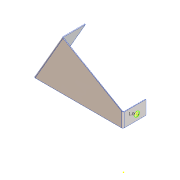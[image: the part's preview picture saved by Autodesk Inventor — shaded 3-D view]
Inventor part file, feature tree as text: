
AUTODESK INVENTOR PART (.ipt)
format: ipt  version: 2016 (Build 200138000, 138)  size: 200,704 bytes
history: native  units: in
note: dims shown in document units (in); Inventor stores cm internally (conversion verified against a paired STEP export)
features: reference x11, sheet_metal_op x7, sketch x6, other x6, fillet x1
ambient origin geometry x8: Origin, YZ Plane, XZ Plane, XY Plane, X Axis, Y Axis, Z Axis, Center Point
bodies: Solid1 (feature_tree)
feature tree (31):
  sheet_metal_op  "Face1"
  sheet_metal_op  "Flange1"
  sketch  "Sketch5"  dims[d8=3.0in]
  sheet_metal_op  "Flange2"
  fillet  "Fillet1"  Radius=30.0in
  sketch  "Sketch7"  dims[d10=90.0deg d11=13.0167in d12=0.125in d13=0.0in d14=0.125in d15=0.0625in d16=0.25in d17=0.125in d18=5.0in d19=90.0deg d20=0.125in d21=0.5in d22=0.125in d23=0.125in d24=0.125in d25=0.0625in d26=0.25in d27=0.125in d28=5.0in d29=90.0deg d30=0.125in d31=0.5in d32=0.125in d33=0.125in d36=1.063in d37=0.125in d38=0.0in d39=0.125in]
  sketch  "Sketch1"  dims[d1=30.0in]
  other  "Plate1"
  sketch  "Sketch3"  dims[d2=0.125in]
  reference  "Reference12"
  reference  "Reference13"
  reference  "Reference14"
  sketch  "Sketch4"  dims[d7=60.0deg]
  other  "Plate2"
  sheet_metal_op  "Bend1"
  sheet_metal_op  "Corner1"
  reference  "Reference15"
  reference  "Reference16"
  reference  "Reference17"
  sketch  "Sketch6"  dims[d9=180.0deg]
  other  "Plate3"
  sheet_metal_op  "Bend2"
  sheet_metal_op  "Corner2"
  reference  "Reference18"
  reference  "Reference19"
  reference  "Reference20"
  reference  "Reference21"
  reference  "Reference22"
  other  "Cut1"
  other  "Cut2"
  other  "Definition1"
